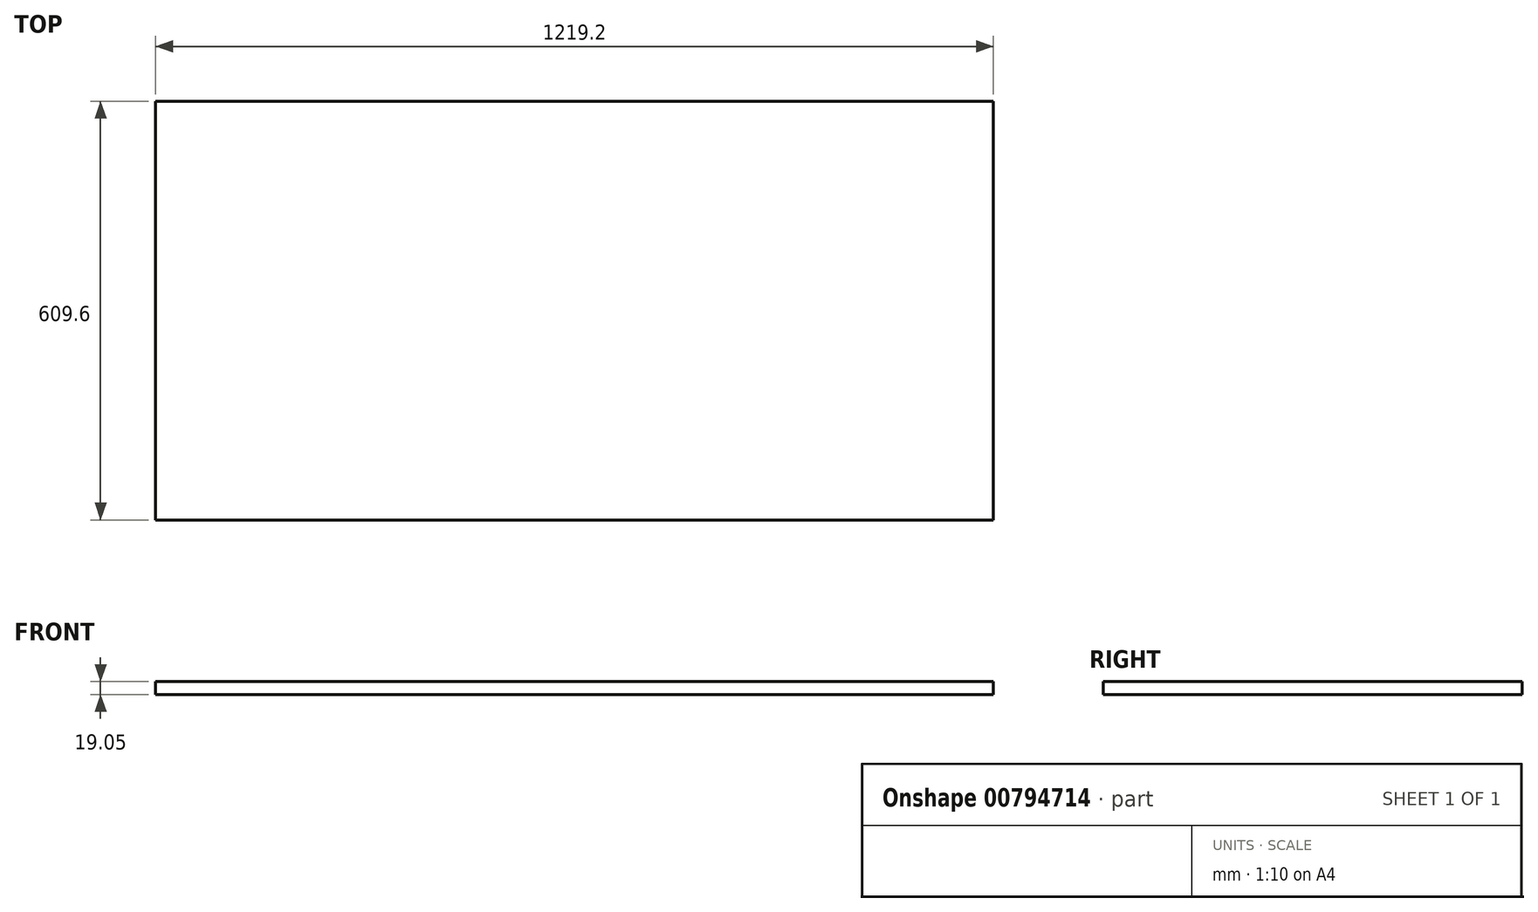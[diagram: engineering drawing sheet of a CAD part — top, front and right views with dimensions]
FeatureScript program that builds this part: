
annotation { "Feature Type Name" : "Feature", "Feature Type Description" : "" }
export const myFeature = defineFeature(function(context is Context, id is Id, definition is map)
    precondition{}
    {
        {
            var Q0;
            Q0=qCreatedBy(makeId("Top.planeOp"),FACE);
            var sketch = newSketch(context, id + "F0", { "sketchPlane" : qUnion([Q0])});
            skLineSegment(sketch, "E0.bottom", {"start": v(609.6, -304.8) * mm, "end": v(-609.6, -304.8) * mm});
            skLineSegment(sketch, "E0.top", {"start": v(609.6, 304.8) * mm, "end": v(-609.6, 304.8) * mm});
            skLineSegment(sketch, "E0.left", {"start": v(609.6, -304.8) * mm, "end": v(609.6, 304.8) * mm});
            skLineSegment(sketch, "E0.right", {"start": v(-609.6, -304.8) * mm, "end": v(-609.6, 304.8) * mm});
            skPoint(sketch, "E0.middle", {"position": v(0, 0) * mm});
            skSolve(sketch);
        }
        {
            var Q0;
            Q0=makeQuery(id+"F0.imprint","IMPRINT",FACE,{"disambiguationData":[TD([[makeQuery(id+"F0.imprint","IMPRINT",EDGE,{"derivedFrom":sQuery(id+"F0.wireOp",EDGE,"E0.bottom")}),-1.0]])]});
            extrude(context, id + "F1", {"entities" : qUnion([Q0]), "depth" : 19.05 * mm, "offsetDistance" : 25.4 * mm});
        }
    });
